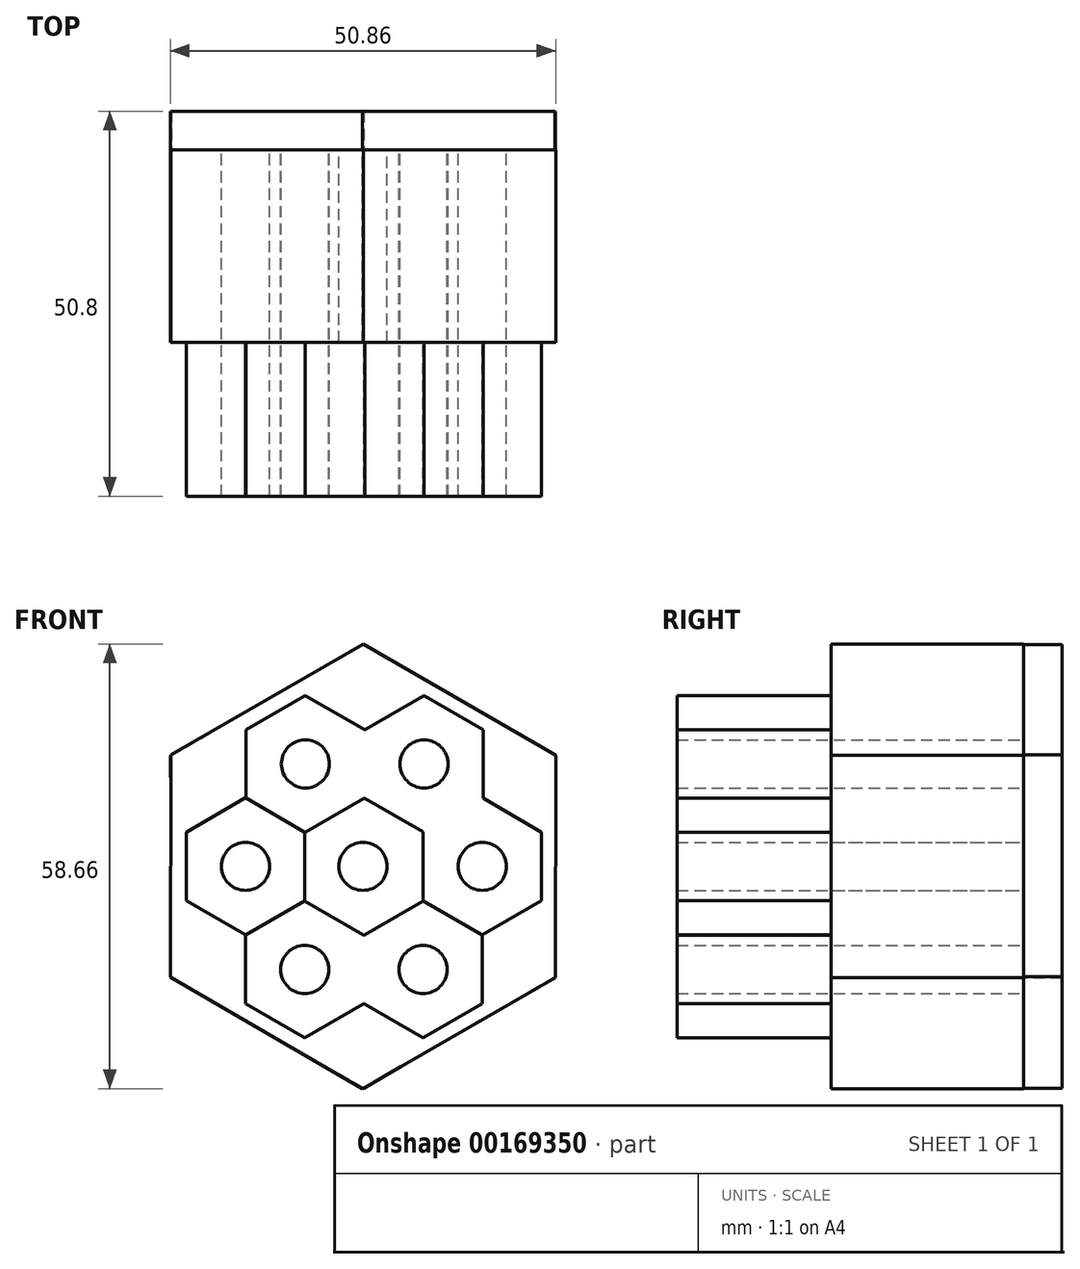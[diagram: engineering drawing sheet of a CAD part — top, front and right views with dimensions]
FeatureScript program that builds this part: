
annotation { "Feature Type Name" : "Feature", "Feature Type Description" : "" }
export const myFeature = defineFeature(function(context is Context, id is Id, definition is map)
    precondition{}
    {
        {
            var Q0;
            Q0=qCreatedBy(makeId("Front.planeOp"),FACE);
            var sketch = newSketch(context, id + "F0", { "sketchPlane" : qUnion([Q0])});
            skCircle(sketch, "E0.cCircle", {"center": v(0, 0) * mm, "radius": 25.4 * mm, "construction": true});
            skLineSegment(sketch, "E0.0", {"start": v(-25.37, 14.7) * mm, "end": v(0.05, 29.33) * mm});
            skLineSegment(sketch, "E0.1", {"start": v(0.05, 29.33) * mm, "end": v(25.43, 14.62) * mm});
            skLineSegment(sketch, "E0.2", {"start": v(25.43, 14.62) * mm, "end": v(25.37, -14.7) * mm});
            skLineSegment(sketch, "E0.3", {"start": v(25.37, -14.7) * mm, "end": v(-0.05, -29.33) * mm});
            skLineSegment(sketch, "E0.4", {"start": v(-0.05, -29.33) * mm, "end": v(-25.43, -14.62) * mm});
            skLineSegment(sketch, "E0.5", {"start": v(-25.43, -14.62) * mm, "end": v(-25.37, 14.7) * mm});
            skPoint(sketch, "E0.0.midPoint", {"position": v(-12.66, 22.02) * mm});
            skCircle(sketch, "E1.cCircle", {"center": v(0, 0) * mm, "radius": 7.82 * mm, "construction": true});
            skLineSegment(sketch, "E1.0", {"start": v(7.82, -4.52) * mm, "end": v(0, -9.03) * mm});
            skLineSegment(sketch, "E1.1", {"start": v(0, -9.03) * mm, "end": v(-7.82, -4.52) * mm});
            skLineSegment(sketch, "E1.2", {"start": v(-7.82, -4.52) * mm, "end": v(-7.82, 4.52) * mm});
            skLineSegment(sketch, "E1.3", {"start": v(-7.82, 4.52) * mm, "end": v(0, 9.03) * mm});
            skLineSegment(sketch, "E1.4", {"start": v(0, 9.03) * mm, "end": v(7.82, 4.52) * mm});
            skLineSegment(sketch, "E1.5", {"start": v(7.82, 4.52) * mm, "end": v(7.82, -4.52) * mm});
            skPoint(sketch, "E1.0.midPoint", {"position": v(3.91, -6.78) * mm});
            skCircle(sketch, "E2.cCircle", {"center": v(0, 0) * mm, "radius": 23.47 * mm, "construction": true});
            skLineSegment(sketch, "E2.0", {"start": v(-23.61, 13.3) * mm, "end": v(-0.29, 27.1) * mm});
            skLineSegment(sketch, "E2.1", {"start": v(-0.29, 27.1) * mm, "end": v(23.32, 13.8) * mm});
            skLineSegment(sketch, "E2.2", {"start": v(23.32, 13.8) * mm, "end": v(23.61, -13.3) * mm});
            skLineSegment(sketch, "E2.3", {"start": v(23.61, -13.3) * mm, "end": v(0.29, -27.1) * mm});
            skLineSegment(sketch, "E2.4", {"start": v(0.29, -27.1) * mm, "end": v(-23.32, -13.8) * mm});
            skLineSegment(sketch, "E2.5", {"start": v(-23.32, -13.8) * mm, "end": v(-23.61, 13.3) * mm});
            skPoint(sketch, "E2.0.midPoint", {"position": v(-11.95, 20.2) * mm});
            skSolve(sketch);
        }
        {
            var Q0;
            Q0=makeQuery(id+"F0.imprint","IMPRINT",FACE,{"disambiguationData":[TD([[makeQuery(id+"F0.imprint","IMPRINT",EDGE,{"derivedFrom":sQuery(id+"F0.wireOp",EDGE,"E0.0")}),1.0]])]});
            var Q1;
            Q1=makeQuery(id+"F0.imprint","IMPRINT",FACE,{"disambiguationData":[TD([[makeQuery(id+"F0.imprint","IMPRINT",EDGE,{"derivedFrom":sQuery(id+"F0.wireOp",EDGE,"E0.0")}),-1.0]])]});
            var Q2;
            Q2=makeQuery(id+"F0.imprint","IMPRINT",FACE,{"disambiguationData":[TD([[makeQuery(id+"F0.imprint","IMPRINT",EDGE,{"derivedFrom":sQuery(id+"F0.wireOp",EDGE,"E1.0")}),-1.0]])]});
            var Q3;
            Q3=makeQuery(id+"F0.imprint","IMPRINT",FACE,{"disambiguationData":[TD([[makeQuery(id+"F0.imprint","IMPRINT",EDGE,{"derivedFrom":sQuery(id+"F0.wireOp",EDGE,"E1.0")}),1.0]])]});
            extrude(context, id + "F1", {"entities" : qUnion([Q0, Q1, Q2, Q3]), "depth" : 25.4 * mm});
        }
        {
            var Q0;
            Q0=qCreatedBy(makeId("Front.planeOp"),FACE);
            var sketch = newSketch(context, id + "F2", { "sketchPlane" : qUnion([Q0])});
            skCircle(sketch, "E3.cCircle", {"center": v(-15.51, 0) * mm, "radius": 7.82 * mm, "construction": true});
            skLineSegment(sketch, "E3.0", {"start": v(-7.69, -4.52) * mm, "end": v(-15.51, -9.03) * mm});
            skLineSegment(sketch, "E3.1", {"start": v(-15.51, -9.03) * mm, "end": v(-23.33, -4.52) * mm});
            skLineSegment(sketch, "E3.2", {"start": v(-23.33, -4.52) * mm, "end": v(-23.33, 4.52) * mm});
            skLineSegment(sketch, "E3.3", {"start": v(-23.33, 4.52) * mm, "end": v(-15.51, 9.03) * mm});
            skLineSegment(sketch, "E3.4", {"start": v(-15.51, 9.03) * mm, "end": v(-7.69, 4.52) * mm});
            skLineSegment(sketch, "E3.5", {"start": v(-7.69, 4.52) * mm, "end": v(-7.69, -4.52) * mm});
            skPoint(sketch, "E3.0.midPoint", {"position": v(-11.6, -6.78) * mm});
            skCircle(sketch, "E4.cCircle", {"center": v(-7.6, 13.52) * mm, "radius": 7.82 * mm, "construction": true});
            skLineSegment(sketch, "E4.0", {"start": v(0.22, 18.04) * mm, "end": v(0.22, 9) * mm});
            skLineSegment(sketch, "E4.1", {"start": v(0.22, 9) * mm, "end": v(-7.6, 4.49) * mm});
            skLineSegment(sketch, "E4.2", {"start": v(-7.6, 4.49) * mm, "end": v(-15.43, 9) * mm});
            skLineSegment(sketch, "E4.3", {"start": v(-15.43, 9) * mm, "end": v(-15.43, 18.04) * mm});
            skLineSegment(sketch, "E4.4", {"start": v(-15.43, 18.04) * mm, "end": v(-7.6, 22.56) * mm});
            skLineSegment(sketch, "E4.5", {"start": v(-7.6, 22.56) * mm, "end": v(0.22, 18.04) * mm});
            skPoint(sketch, "E4.0.midPoint", {"position": v(0.22, 13.52) * mm});
            skCircle(sketch, "E5.cCircle", {"center": v(-7.69, -13.61) * mm, "radius": 7.82 * mm, "construction": true});
            skLineSegment(sketch, "E5.0", {"start": v(0.13, -18.13) * mm, "end": v(-7.69, -22.65) * mm});
            skLineSegment(sketch, "E5.1", {"start": v(-7.69, -22.65) * mm, "end": v(-15.51, -18.13) * mm});
            skLineSegment(sketch, "E5.2", {"start": v(-15.51, -18.13) * mm, "end": v(-15.51, -9.1) * mm});
            skLineSegment(sketch, "E5.3", {"start": v(-15.51, -9.1) * mm, "end": v(-7.69, -4.58) * mm});
            skLineSegment(sketch, "E5.4", {"start": v(-7.69, -4.58) * mm, "end": v(0.13, -9.1) * mm});
            skLineSegment(sketch, "E5.5", {"start": v(0.13, -9.1) * mm, "end": v(0.13, -18.13) * mm});
            skPoint(sketch, "E5.0.midPoint", {"position": v(-3.78, -20.39) * mm});
            skCircle(sketch, "E6.cCircle", {"center": v(15.74, 0) * mm, "radius": 7.82 * mm, "construction": true});
            skLineSegment(sketch, "E6.0", {"start": v(23.56, -4.52) * mm, "end": v(15.74, -9.03) * mm});
            skLineSegment(sketch, "E6.1", {"start": v(15.74, -9.03) * mm, "end": v(7.92, -4.52) * mm});
            skLineSegment(sketch, "E6.2", {"start": v(7.92, -4.52) * mm, "end": v(7.92, 4.52) * mm});
            skLineSegment(sketch, "E6.3", {"start": v(7.92, 4.52) * mm, "end": v(15.74, 9.03) * mm});
            skLineSegment(sketch, "E6.4", {"start": v(15.74, 9.03) * mm, "end": v(23.56, 4.52) * mm});
            skLineSegment(sketch, "E6.5", {"start": v(23.56, 4.52) * mm, "end": v(23.56, -4.52) * mm});
            skPoint(sketch, "E6.0.midPoint", {"position": v(19.65, -6.78) * mm});
            skCircle(sketch, "E7.cCircle", {"center": v(7.92, -13.61) * mm, "radius": 7.82 * mm, "construction": true});
            skLineSegment(sketch, "E7.0", {"start": v(15.74, -18.13) * mm, "end": v(7.92, -22.65) * mm});
            skLineSegment(sketch, "E7.1", {"start": v(7.92, -22.65) * mm, "end": v(0.1, -18.13) * mm});
            skLineSegment(sketch, "E7.2", {"start": v(0.1, -18.13) * mm, "end": v(0.1, -9.1) * mm});
            skLineSegment(sketch, "E7.3", {"start": v(0.1, -9.1) * mm, "end": v(7.92, -4.58) * mm});
            skLineSegment(sketch, "E7.4", {"start": v(7.92, -4.58) * mm, "end": v(15.74, -9.1) * mm});
            skLineSegment(sketch, "E7.5", {"start": v(15.74, -9.1) * mm, "end": v(15.74, -18.13) * mm});
            skPoint(sketch, "E7.0.midPoint", {"position": v(11.83, -20.39) * mm});
            skCircle(sketch, "E8.cCircle", {"center": v(8.05, 13.5) * mm, "radius": 7.82 * mm, "construction": true});
            skLineSegment(sketch, "E8.0", {"start": v(15.87, 8.98) * mm, "end": v(8.05, 4.47) * mm});
            skLineSegment(sketch, "E8.1", {"start": v(8.05, 4.47) * mm, "end": v(0.23, 8.98) * mm});
            skLineSegment(sketch, "E8.2", {"start": v(0.23, 8.98) * mm, "end": v(0.23, 18.02) * mm});
            skLineSegment(sketch, "E8.3", {"start": v(0.23, 18.02) * mm, "end": v(8.05, 22.53) * mm});
            skLineSegment(sketch, "E8.4", {"start": v(8.05, 22.53) * mm, "end": v(15.87, 18.02) * mm});
            skLineSegment(sketch, "E8.5", {"start": v(15.87, 18.02) * mm, "end": v(15.87, 8.98) * mm});
            skPoint(sketch, "E8.0.midPoint", {"position": v(11.96, 6.73) * mm});
            skSolve(sketch);
        }
        {
            var Q0;
            Q0 = qSketchRegion(id + "F2", true);
            extrude(context, id + "F3", {"entities" : qUnion([Q0]), "operationType" : NewBodyOperationType.ADD, "depth" : 45.72 * mm});
        }
        {
            var Q0;
            Q0=sQuery(id+"F2.wireOp",VERTEX,"E4.cCircle.center");
            var Q1;
            Q1=sQuery(id+"F2.wireOp",VERTEX,"E3.cCircle.center");
            var Q2;
            Q2=sQuery(id+"F2.wireOp",VERTEX,"E5.cCircle.center");
            var Q3;
            Q3=sQuery(id+"F2.wireOp",VERTEX,"E7.cCircle.center");
            var Q4;
            Q4=sQuery(id+"F2.wireOp",VERTEX,"E6.cCircle.center");
            var Q5;
            Q5=sQuery(id+"F2.wireOp",VERTEX,"E8.cCircle.center");
            var Q6;
            Q6=sQuery(id+"F0.wireOp",VERTEX,"E1.cCircle.center");
            var Q7;
            Q7=makeQuery(id+"F1.opExtrude","SWEPT_BODY",BODY,{"disambiguationData":[OSD([sQuery(id+"F0.wireOp",EDGE,"E0.0"),sQuery(id+"F0.wireOp",EDGE,"E0.1"),sQuery(id+"F0.wireOp",EDGE,"E0.2"),sQuery(id+"F0.wireOp",EDGE,"E0.3"),sQuery(id+"F0.wireOp",EDGE,"E0.4"),sQuery(id+"F0.wireOp",EDGE,"E0.5")])]});
            hole(context, id + "F4", {"style" : HoleStyle.SIMPLE, "endStyle" : HoleEndStyle.THROUGH, "oppositeDirection" : true, "holeDiameter" : 6.35 * mm, "locations" : qUnion([Q0, Q1, Q2, Q3, Q4, Q5, Q6]), "scope" : qUnion([Q7]), "isTappedThrough" : true});
        }
        {
            var Q0;
            Q0=qCreatedBy(makeId("Front.planeOp"),FACE);
            var sketch = newSketch(context, id + "F5", { "sketchPlane" : qUnion([Q0])});
            skCircle(sketch, "E9.cCircle", {"center": v(0, 0) * mm, "radius": 25.36 * mm, "construction": true});
            skLineSegment(sketch, "E9.0", {"start": v(-0.1, 29.28) * mm, "end": v(25.31, 14.72) * mm});
            skLineSegment(sketch, "E9.1", {"start": v(25.31, 14.72) * mm, "end": v(25.4, -14.56) * mm});
            skLineSegment(sketch, "E9.2", {"start": v(25.4, -14.56) * mm, "end": v(0.1, -29.28) * mm});
            skLineSegment(sketch, "E9.3", {"start": v(0.1, -29.28) * mm, "end": v(-25.31, -14.72) * mm});
            skLineSegment(sketch, "E9.4", {"start": v(-25.31, -14.72) * mm, "end": v(-25.4, 14.56) * mm});
            skLineSegment(sketch, "E9.5", {"start": v(-25.4, 14.56) * mm, "end": v(-0.1, 29.28) * mm});
            skPoint(sketch, "E9.0.midPoint", {"position": v(12.61, 22) * mm});
            skSolve(sketch);
        }
        {
            var Q0;
            Q0 = qSketchRegion(id + "F5", true);
            extrude(context, id + "F6", {"entities" : qUnion([Q0]), "operationType" : NewBodyOperationType.ADD, "oppositeDirection" : true, "depth" : 5.08 * mm});
        }
    });
